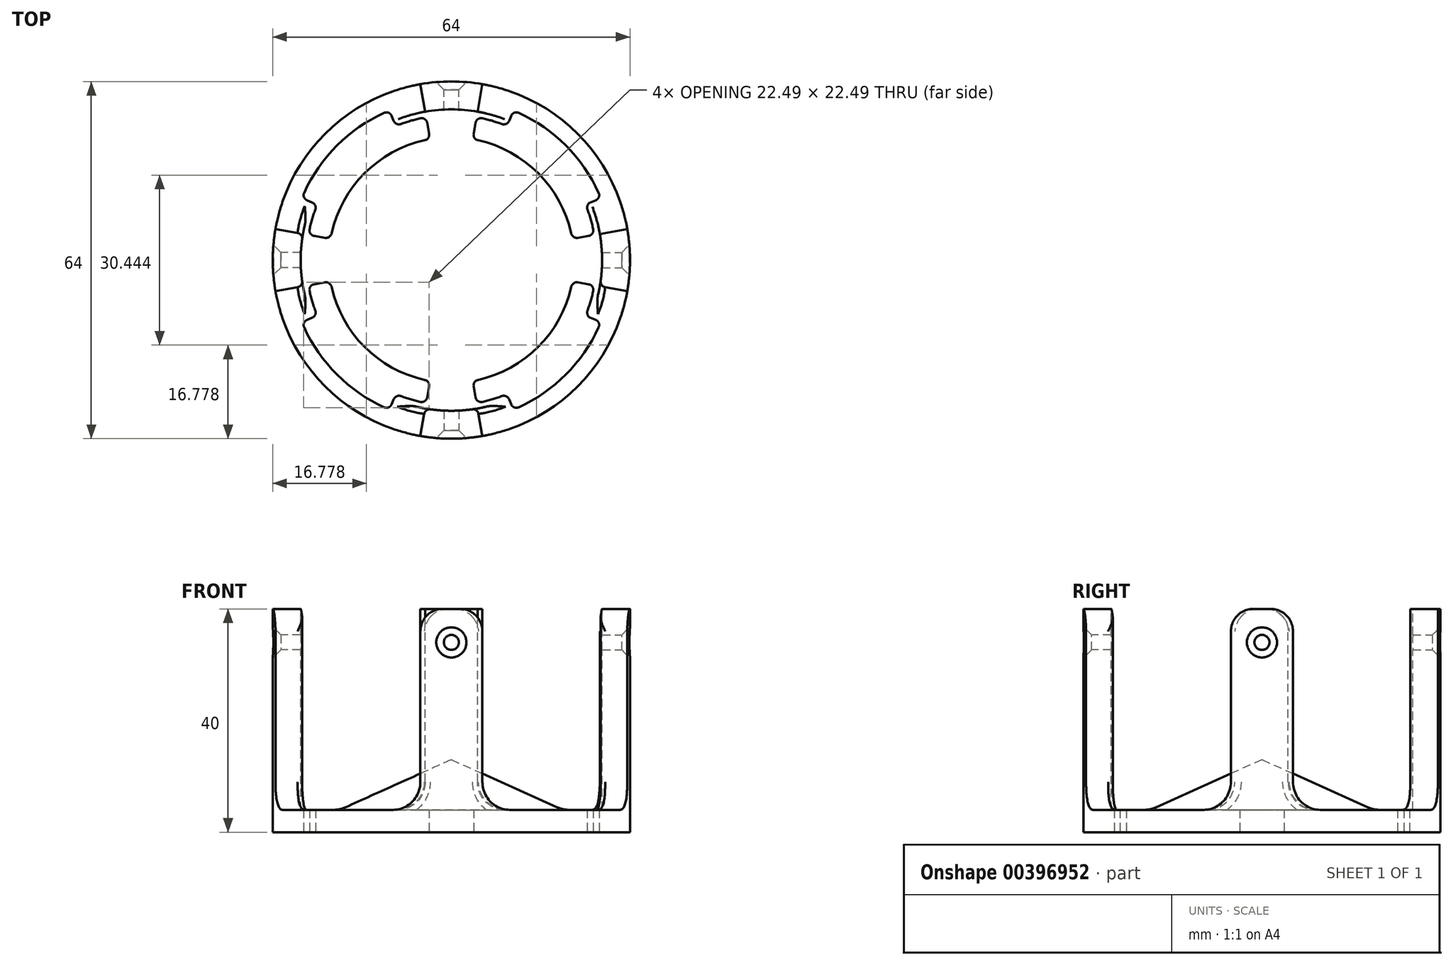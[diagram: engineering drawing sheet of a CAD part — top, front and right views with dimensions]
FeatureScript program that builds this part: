
annotation { "Feature Type Name" : "Feature", "Feature Type Description" : "" }
export const myFeature = defineFeature(function(context is Context, id is Id, definition is map)
    precondition{}
    {
        {
            var Q0;
            Q0=qCreatedBy(makeId("Front.planeOp"),FACE);
            var sketch = newSketch(context, id + "F0", { "sketchPlane" : qUnion([Q0])});
            skLineSegment(sketch, "E0", {"start": v(32, 0) * mm, "end": v(32, 40) * mm});
            skLineSegment(sketch, "E1", {"start": v(32, 40) * mm, "end": v(27, 40) * mm});
            skLineSegment(sketch, "E2", {"start": v(27, 40) * mm, "end": v(27, 4) * mm});
            skLineSegment(sketch, "E3", {"start": v(27, 4) * mm, "end": v(20, 4) * mm});
            skLineSegment(sketch, "E4", {"start": v(20, 4) * mm, "end": v(0, 13) * mm});
            skLineSegment(sketch, "E5", {"start": v(0, 13) * mm, "end": v(0, 0) * mm});
            skLineSegment(sketch, "E6", {"start": v(0, 0) * mm, "end": v(32, 0) * mm});
            skSolve(sketch);
        }
        {
            var Q0;
            Q0=makeQuery(id+"F0.imprint","IMPRINT",FACE,{"disambiguationData":[TD([[makeQuery(id+"F0.imprint","IMPRINT",EDGE,{"derivedFrom":sQuery(id+"F0.wireOp",EDGE,"E0")}),1.0]])]});
            var Q1;
            Q1=sQuery(id+"F0.wireOp",EDGE,"E5");
            revolve(context, id + "F1", {"entities" : qUnion([Q0]), "axis" : qUnion([Q1]), "revolveType" : RevolveType.FULL});
        }
        {
            var Q0;
            Q0=makeQuery(id+"F1.opRevolve","SWEPT_FACE",FACE,{"disambiguationData":[OSD([sQuery(id+"F0.wireOp",EDGE,"E1")])]});
            var sketch = newSketch(context, id + "F2", { "sketchPlane" : qUnion([Q0])});
            skLineSegment(sketch, "E7", {"start": v(-5.56, 31.51) * mm, "end": v(-4.69, 26.59) * mm});
            skLineSegment(sketch, "E8", {"start": v(4.69, 26.59) * mm, "end": v(5.56, 31.51) * mm});
            skLineSegment(sketch, "E9", {"start": v(31.51, 5.56) * mm, "end": v(26.59, 4.69) * mm});
            skLineSegment(sketch, "E10", {"start": v(31.51, -5.56) * mm, "end": v(26.59, -4.69) * mm});
            skLineSegment(sketch, "E11", {"start": v(4.69, -26.59) * mm, "end": v(5.56, -31.51) * mm});
            skLineSegment(sketch, "E12", {"start": v(-4.69, -26.59) * mm, "end": v(-5.56, -31.51) * mm});
            skLineSegment(sketch, "E13", {"start": v(-31.51, -5.56) * mm, "end": v(-26.59, -4.69) * mm});
            skLineSegment(sketch, "E14", {"start": v(-31.51, 5.56) * mm, "end": v(-26.59, 4.69) * mm});
            skArc(sketch, "E15", {"start": v(-5.56, 31.51) * mm, "mid": v(-22.63, 22.63) * mm, "end": v(-31.51, 5.56) * mm});
            skArc(sketch, "E16", {"start": v(-4.69, 26.59) * mm, "mid": v(-19.1, 19.1) * mm, "end": v(-26.59, 4.69) * mm});
            skArc(sketch, "E17.trimOffspring", {"start": v(26.59, 4.69) * mm, "mid": v(19.1, 19.1) * mm, "end": v(4.69, 26.59) * mm});
            skArc(sketch, "E18.trimOffspring", {"start": v(31.51, 5.56) * mm, "mid": v(22.63, 22.63) * mm, "end": v(5.56, 31.51) * mm});
            skArc(sketch, "E19.trimOffspring", {"start": v(4.69, -26.59) * mm, "mid": v(19.1, -19.1) * mm, "end": v(26.59, -4.69) * mm});
            skArc(sketch, "E20.trimOffspring", {"start": v(-31.51, -5.56) * mm, "mid": v(-22.63, -22.63) * mm, "end": v(-5.56, -31.51) * mm});
            skArc(sketch, "E21.trimOffspring", {"start": v(-26.59, -4.69) * mm, "mid": v(-19.1, -19.1) * mm, "end": v(-4.69, -26.59) * mm});
            skSolve(sketch);
        }
        {
            var Q0;
            Q0=makeQuery(id+"F2.imprint","IMPRINT",FACE,{"disambiguationData":[TD([[makeQuery(id+"F2.imprint","IMPRINT",EDGE,{"derivedFrom":sQuery(id+"F2.wireOp",EDGE,"E7")}),-1.0]])]});
            var Q1;
            Q1=makeQuery(id+"F2.imprint","IMPRINT",FACE,{"disambiguationData":[TD([[makeQuery(id+"F2.imprint","IMPRINT",EDGE,{"derivedFrom":sQuery(id+"F2.wireOp",EDGE,"E8")}),-1.0]])]});
            var Q2;
            {var subQ0=sQuery(id+"F2.wireOp",EDGE,"E10");Q2=makeQuery(id+"F2.imprint","IMPRINT",FACE,{"disambiguationData":[TD([[makeQuery(id+"F2.imprint","IMPRINT",EDGE,{"derivedFrom":subQ0}),1.0]])]});}
            var Q3;
            Q3=makeQuery(id+"F2.imprint","IMPRINT",FACE,{"disambiguationData":[TD([[makeQuery(id+"F2.imprint","IMPRINT",EDGE,{"derivedFrom":sQuery(id+"F2.wireOp",EDGE,"E12")}),-1.0]])]});
            var Q4;
            Q4=makeQuery(id+"F1.opRevolve","SWEPT_FACE",FACE,{"disambiguationData":[OSD([sQuery(id+"F0.wireOp",EDGE,"E3")])]});
            extrude(context, id + "F3", {"entities" : qUnion([Q0, Q1, Q2, Q3]), "operationType" : NewBodyOperationType.REMOVE, "endBound" : BoundingType.UP_TO_SURFACE, "oppositeDirection" : true, "endBoundEntityFace" : qUnion([Q4]), "depth" : 25 * mm});
        }
        {
            var Q0;
            Q0=makeQuery(id+"F3.boolean.opBoolean","COPY",EDGE,{"derivedFrom":makeQuery(id+"F3.opExtrude","CAP_EDGE",EDGE,{"disambiguationData":[OSD([sQuery(id+"F2.wireOp",EDGE,"E11")])],"isStart":false})});
            var Q1;
            Q1=makeQuery(id+"F3.boolean.opBoolean","COPY",EDGE,{"derivedFrom":makeQuery(id+"F3.opExtrude","CAP_EDGE",EDGE,{"disambiguationData":[OSD([sQuery(id+"F2.wireOp",EDGE,"E10")])],"isStart":false})});
            var Q2;
            Q2=makeQuery(id+"F3.boolean.opBoolean","COPY",EDGE,{"derivedFrom":makeQuery(id+"F3.opExtrude","CAP_EDGE",EDGE,{"disambiguationData":[OSD([sQuery(id+"F2.wireOp",EDGE,"E9")])],"isStart":false})});
            var Q3;
            Q3=makeQuery(id+"F3.boolean.opBoolean","COPY",EDGE,{"derivedFrom":makeQuery(id+"F3.opExtrude","CAP_EDGE",EDGE,{"disambiguationData":[OSD([sQuery(id+"F2.wireOp",EDGE,"E8")])],"isStart":false})});
            var Q4;
            Q4=makeQuery(id+"F3.boolean.opBoolean","COPY",EDGE,{"derivedFrom":makeQuery(id+"F3.opExtrude","CAP_EDGE",EDGE,{"disambiguationData":[OSD([sQuery(id+"F2.wireOp",EDGE,"E7")])],"isStart":false})});
            var Q5;
            Q5=makeQuery(id+"F3.boolean.opBoolean","COPY",EDGE,{"derivedFrom":makeQuery(id+"F3.opExtrude","CAP_EDGE",EDGE,{"disambiguationData":[OSD([sQuery(id+"F2.wireOp",EDGE,"E14")])],"isStart":false})});
            var Q6;
            Q6=makeQuery(id+"F3.boolean.opBoolean","COPY",EDGE,{"derivedFrom":makeQuery(id+"F3.opExtrude","CAP_EDGE",EDGE,{"disambiguationData":[OSD([sQuery(id+"F2.wireOp",EDGE,"E13")])],"isStart":false})});
            var Q7;
            Q7=makeQuery(id+"F3.boolean.opBoolean","COPY",EDGE,{"derivedFrom":makeQuery(id+"F3.opExtrude","CAP_EDGE",EDGE,{"disambiguationData":[OSD([sQuery(id+"F2.wireOp",EDGE,"E12")])],"isStart":false})});
            fillet(context, id + "F4", {"entities" : qUnion([Q0, Q1, Q2, Q3, Q4, Q5, Q6, Q7]), "radius" : 5 * mm, "tangentPropagation" : true, "allowEdgeOverflow" : false});
        }
        {
            var Q0;
            Q0=makeQuery(id+"F1.opRevolve","SWEPT_EDGE",EDGE,{"disambiguationData":[OSD([sQuery(id+"F0.wireOp",EDGE,"E3"),sQuery(id+"F0.wireOp",EDGE,"E4")])]});
            fillet(context, id + "F5", {"entities" : qUnion([Q0]), "radius" : 5 * mm, "tangentPropagation" : true, "allowEdgeOverflow" : false});
        }
        {
            var Q0;
            Q0=makeQuery(id+"F3.boolean.opBoolean","COPY",EDGE,{"derivedFrom":makeQuery(id+"F3.opExtrude","SWEPT_EDGE",EDGE,{"disambiguationData":[OSD([sQuery(id+"F0.wireOp",EDGE,"E0"),sQuery(id+"F0.wireOp",EDGE,"E1"),sQuery(id+"F2.wireOp",EDGE,"E13"),sQuery(id+"F2.wireOp",EDGE,"E20.trimOffspring")])]})});
            var Q1;
            Q1=makeQuery(id+"F3.boolean.opBoolean","COPY",EDGE,{"derivedFrom":makeQuery(id+"F3.opExtrude","SWEPT_EDGE",EDGE,{"disambiguationData":[OSD([sQuery(id+"F0.wireOp",EDGE,"E0"),sQuery(id+"F0.wireOp",EDGE,"E1"),sQuery(id+"F2.wireOp",EDGE,"E14"),sQuery(id+"F2.wireOp",EDGE,"E15")])]})});
            var Q2;
            Q2=makeQuery(id+"F3.boolean.opBoolean","COPY",EDGE,{"derivedFrom":makeQuery(id+"F3.opExtrude","SWEPT_EDGE",EDGE,{"disambiguationData":[OSD([sQuery(id+"F0.wireOp",EDGE,"E0"),sQuery(id+"F0.wireOp",EDGE,"E1"),sQuery(id+"F2.wireOp",EDGE,"E11")])]})});
            var Q3;
            Q3=makeQuery(id+"F3.boolean.opBoolean","COPY",EDGE,{"derivedFrom":makeQuery(id+"F3.opExtrude","SWEPT_EDGE",EDGE,{"disambiguationData":[OSD([sQuery(id+"F0.wireOp",EDGE,"E0"),sQuery(id+"F0.wireOp",EDGE,"E1"),sQuery(id+"F2.wireOp",EDGE,"E8"),sQuery(id+"F2.wireOp",EDGE,"E18.trimOffspring")])]})});
            var Q4;
            Q4=makeQuery(id+"F3.boolean.opBoolean","COPY",EDGE,{"derivedFrom":makeQuery(id+"F3.opExtrude","SWEPT_EDGE",EDGE,{"disambiguationData":[OSD([sQuery(id+"F0.wireOp",EDGE,"E1"),sQuery(id+"F0.wireOp",EDGE,"E2"),sQuery(id+"F2.wireOp",EDGE,"E11"),sQuery(id+"F2.wireOp",EDGE,"E19.trimOffspring")])]})});
            var Q5;
            Q5=makeQuery(id+"F3.boolean.opBoolean","COPY",EDGE,{"derivedFrom":makeQuery(id+"F3.opExtrude","SWEPT_EDGE",EDGE,{"disambiguationData":[OSD([sQuery(id+"F0.wireOp",EDGE,"E1"),sQuery(id+"F0.wireOp",EDGE,"E2"),sQuery(id+"F2.wireOp",EDGE,"E10"),sQuery(id+"F2.wireOp",EDGE,"E19.trimOffspring")])]})});
            var Q6;
            Q6=makeQuery(id+"F3.boolean.opBoolean","COPY",EDGE,{"derivedFrom":makeQuery(id+"F3.opExtrude","SWEPT_EDGE",EDGE,{"disambiguationData":[OSD([sQuery(id+"F0.wireOp",EDGE,"E1"),sQuery(id+"F0.wireOp",EDGE,"E2"),sQuery(id+"F2.wireOp",EDGE,"E8"),sQuery(id+"F2.wireOp",EDGE,"E17.trimOffspring")])]})});
            var Q7;
            Q7=makeQuery(id+"F3.boolean.opBoolean","COPY",EDGE,{"derivedFrom":makeQuery(id+"F3.opExtrude","SWEPT_EDGE",EDGE,{"disambiguationData":[OSD([sQuery(id+"F0.wireOp",EDGE,"E1"),sQuery(id+"F0.wireOp",EDGE,"E2"),sQuery(id+"F2.wireOp",EDGE,"E7"),sQuery(id+"F2.wireOp",EDGE,"E16")])]})});
            var Q8;
            Q8=makeQuery(id+"F3.boolean.opBoolean","COPY",EDGE,{"derivedFrom":makeQuery(id+"F3.opExtrude","SWEPT_EDGE",EDGE,{"disambiguationData":[OSD([sQuery(id+"F0.wireOp",EDGE,"E1"),sQuery(id+"F0.wireOp",EDGE,"E2"),sQuery(id+"F2.wireOp",EDGE,"E14"),sQuery(id+"F2.wireOp",EDGE,"E16")])]})});
            var Q9;
            Q9=makeQuery(id+"F3.boolean.opBoolean","COPY",EDGE,{"derivedFrom":makeQuery(id+"F3.opExtrude","SWEPT_EDGE",EDGE,{"disambiguationData":[OSD([sQuery(id+"F0.wireOp",EDGE,"E1"),sQuery(id+"F0.wireOp",EDGE,"E2"),sQuery(id+"F2.wireOp",EDGE,"E13"),sQuery(id+"F2.wireOp",EDGE,"E21.trimOffspring")])]})});
            var Q10;
            Q10=makeQuery(id+"F3.boolean.opBoolean","COPY",EDGE,{"derivedFrom":makeQuery(id+"F3.opExtrude","SWEPT_EDGE",EDGE,{"disambiguationData":[OSD([sQuery(id+"F0.wireOp",EDGE,"E1"),sQuery(id+"F0.wireOp",EDGE,"E2"),sQuery(id+"F2.wireOp",EDGE,"E12"),sQuery(id+"F2.wireOp",EDGE,"E21.trimOffspring")])]})});
            fillet(context, id + "F6", {"entities" : qUnion([Q0, Q1, Q2, Q3, Q4, Q5, Q6, Q7, Q8, Q9, Q10]), "radius" : 1 * mm, "tangentPropagation" : true, "allowEdgeOverflow" : false});
        }
        {
            var Q0;
            {var subQ0=sQuery(id+"F0.wireOp",EDGE,"E0");var subQ1=sQuery(id+"F0.wireOp",EDGE,"E1");Q0=makeQuery(id+"F3.boolean.opBoolean","SPLIT",EDGE,{"disambiguationData":[TD([makeQuery(id+"F3.opExtrude","SWEPT_FACE",FACE,{"disambiguationData":[OSD([sQuery(id+"F2.wireOp",EDGE,"E11")])]})])],"derivedFrom":makeQuery(id+"F1.opRevolve","SWEPT_EDGE",EDGE,{"disambiguationData":[OSD([subQ0,subQ1])]})});}
            cPoint(context, id + "F7", {"entities" : qUnion([Q0]), "parameter" : 0.5});
        }
        {
            var Q0;
            Q0=qCreatedBy(makeId("Front.planeOp"),FACE);
            var Q1;
            Q1 = qCreatedBy(id + "F7" ,VERTEX);
            cPlane(context, id + "F8", {"entities" : qUnion([Q0, Q1]), "cplaneType" : CPlaneType.PLANE_POINT, "offset" : 25 * mm, "width" : 150 * mm, "height" : 150 * mm});
        }
        {
            var Q0;
            {var subQ0=sQuery(id+"F0.wireOp",EDGE,"E0");var subQ1=sQuery(id+"F0.wireOp",EDGE,"E1");Q0=makeQuery(id+"F3.boolean.opBoolean","SPLIT",EDGE,{"disambiguationData":[TD([makeQuery(id+"F3.opExtrude","SWEPT_FACE",FACE,{"disambiguationData":[OSD([sQuery(id+"F2.wireOp",EDGE,"E9")])]})])],"derivedFrom":makeQuery(id+"F1.opRevolve","SWEPT_EDGE",EDGE,{"disambiguationData":[OSD([subQ0,subQ1])]})});}
            cPoint(context, id + "F9", {"entities" : qUnion([Q0]), "parameter" : 0.5});
        }
        {
            var Q0;
            Q0=qCreatedBy(makeId("Right.planeOp"),FACE);
            var Q1;
            Q1 = qCreatedBy(id + "F9" ,VERTEX);
            cPlane(context, id + "F10", {"entities" : qUnion([Q0, Q1]), "cplaneType" : CPlaneType.PLANE_POINT, "offset" : 25 * mm, "width" : 150 * mm, "height" : 150 * mm});
        }
        {
            var Q0;
            {var subQ0=sQuery(id+"F0.wireOp",EDGE,"E0");var subQ1=sQuery(id+"F0.wireOp",EDGE,"E1");Q0=makeQuery(id+"F3.boolean.opBoolean","SPLIT",EDGE,{"disambiguationData":[TD([makeQuery(id+"F3.opExtrude","SWEPT_FACE",FACE,{"disambiguationData":[OSD([sQuery(id+"F2.wireOp",EDGE,"E7")])]})])],"derivedFrom":makeQuery(id+"F1.opRevolve","SWEPT_EDGE",EDGE,{"disambiguationData":[OSD([subQ0,subQ1])]})});}
            cPoint(context, id + "F11", {"entities" : qUnion([Q0]), "parameter" : 0.5});
        }
        {
            var Q0;
            Q0=qCreatedBy(makeId("Front.planeOp"),FACE);
            var Q1;
            Q1 = qCreatedBy(id + "F11" ,VERTEX);
            cPlane(context, id + "F12", {"entities" : qUnion([Q0, Q1]), "cplaneType" : CPlaneType.PLANE_POINT, "offset" : 25 * mm, "width" : 150 * mm, "height" : 150 * mm});
        }
        {
            var Q0;
            {var subQ0=sQuery(id+"F0.wireOp",EDGE,"E0");var subQ1=sQuery(id+"F0.wireOp",EDGE,"E1");Q0=makeQuery(id+"F3.boolean.opBoolean","SPLIT",EDGE,{"disambiguationData":[TD([makeQuery(id+"F3.opExtrude","SWEPT_FACE",FACE,{"disambiguationData":[OSD([sQuery(id+"F2.wireOp",EDGE,"E13")])]})])],"derivedFrom":makeQuery(id+"F1.opRevolve","SWEPT_EDGE",EDGE,{"disambiguationData":[OSD([subQ0,subQ1])]})});}
            cPoint(context, id + "F13", {"entities" : qUnion([Q0]), "parameter" : 0.5});
        }
        {
            var Q0;
            Q0=qCreatedBy(makeId("Right.planeOp"),FACE);
            var Q1;
            Q1 = qCreatedBy(id + "F13" ,VERTEX);
            cPlane(context, id + "F14", {"entities" : qUnion([Q0, Q1]), "cplaneType" : CPlaneType.PLANE_POINT, "offset" : 25 * mm, "width" : 150 * mm, "height" : 150 * mm});
        }
        {
            var Q0;
            Q0=qCreatedBy(id+"F8.planeOp",FACE);
            var sketch = newSketch(context, id + "F15", { "sketchPlane" : qUnion([Q0])});
            skPoint(sketch, "E22", {"position": v(0, 34) * mm});
            skSolve(sketch);
        }
        {
            var Q0;
            Q0=qCreatedBy(id+"F10.planeOp",FACE);
            var sketch = newSketch(context, id + "F16", { "sketchPlane" : qUnion([Q0])});
            skPoint(sketch, "E23", {"position": v(0, 34) * mm});
            skSolve(sketch);
        }
        {
            var Q0;
            Q0=qCreatedBy(id+"F12.planeOp",FACE);
            var sketch = newSketch(context, id + "F17", { "sketchPlane" : qUnion([Q0])});
            skPoint(sketch, "E24", {"position": v(0, 34) * mm});
            skSolve(sketch);
        }
        {
            var Q0;
            Q0=qCreatedBy(id+"F14.planeOp",FACE);
            var sketch = newSketch(context, id + "F18", { "sketchPlane" : qUnion([Q0])});
            skPoint(sketch, "E25", {"position": v(0, 34) * mm});
            skSolve(sketch);
        }
        {
            var Q0;
            Q0=sQuery(id+"F16.wireOp",VERTEX,"E23");
            var Q1;
            Q1=makeQuery(id+"F1.opRevolve","SWEPT_BODY",BODY,{"disambiguationData":[OSD([sQuery(id+"F0.wireOp",EDGE,"E0"),sQuery(id+"F0.wireOp",EDGE,"E1"),sQuery(id+"F0.wireOp",EDGE,"E2"),sQuery(id+"F0.wireOp",EDGE,"E3"),sQuery(id+"F0.wireOp",EDGE,"E4"),sQuery(id+"F0.wireOp",EDGE,"E5"),sQuery(id+"F0.wireOp",EDGE,"E6")])]});
            hole(context, id + "F19", {"style" : HoleStyle.C_SINK, "endStyle" : HoleEndStyle.BLIND, "holeDiameter" : 2.7 * mm, "cSinkDiameter" : 5.4 * mm, "cSinkAngle" : 90 * degree, "holeDepth" : 12 * mm, "isTappedThrough" : true, "tappedDepth" : 12 * mm, "tapClearance" : 3, "locations" : qUnion([Q0]), "scope" : qUnion([Q1])});
        }
        {
            var Q0;
            Q0=sQuery(id+"F17.wireOp",VERTEX,"E24");
            var Q1;
            Q1=makeQuery(id+"F1.opRevolve","SWEPT_BODY",BODY,{"disambiguationData":[OSD([sQuery(id+"F0.wireOp",EDGE,"E0"),sQuery(id+"F0.wireOp",EDGE,"E1"),sQuery(id+"F0.wireOp",EDGE,"E2"),sQuery(id+"F0.wireOp",EDGE,"E3"),sQuery(id+"F0.wireOp",EDGE,"E4"),sQuery(id+"F0.wireOp",EDGE,"E5"),sQuery(id+"F0.wireOp",EDGE,"E6")])]});
            hole(context, id + "F20", {"style" : HoleStyle.C_SINK, "endStyle" : HoleEndStyle.BLIND, "oppositeDirection" : true, "holeDiameter" : 2.7 * mm, "cSinkDiameter" : 5.4 * mm, "cSinkAngle" : 90 * degree, "holeDepth" : 12 * mm, "isTappedThrough" : true, "tappedDepth" : 12 * mm, "tapClearance" : 3, "locations" : qUnion([Q0]), "scope" : qUnion([Q1])});
        }
        {
            var Q0;
            Q0=sQuery(id+"F18.wireOp",VERTEX,"E25");
            var Q1;
            Q1=makeQuery(id+"F1.opRevolve","SWEPT_BODY",BODY,{"disambiguationData":[OSD([sQuery(id+"F0.wireOp",EDGE,"E0"),sQuery(id+"F0.wireOp",EDGE,"E1"),sQuery(id+"F0.wireOp",EDGE,"E2"),sQuery(id+"F0.wireOp",EDGE,"E3"),sQuery(id+"F0.wireOp",EDGE,"E4"),sQuery(id+"F0.wireOp",EDGE,"E5"),sQuery(id+"F0.wireOp",EDGE,"E6")])]});
            hole(context, id + "F21", {"style" : HoleStyle.C_SINK, "endStyle" : HoleEndStyle.BLIND, "oppositeDirection" : true, "holeDiameter" : 2.7 * mm, "cSinkDiameter" : 5.4 * mm, "cSinkAngle" : 90 * degree, "holeDepth" : 12 * mm, "isTappedThrough" : true, "tappedDepth" : 12 * mm, "tapClearance" : 3, "locations" : qUnion([Q0]), "scope" : qUnion([Q1])});
        }
        {
            var Q0;
            Q0=sQuery(id+"F15.wireOp",VERTEX,"E22");
            var Q1;
            Q1=makeQuery(id+"F1.opRevolve","SWEPT_BODY",BODY,{"disambiguationData":[OSD([sQuery(id+"F0.wireOp",EDGE,"E0"),sQuery(id+"F0.wireOp",EDGE,"E1"),sQuery(id+"F0.wireOp",EDGE,"E2"),sQuery(id+"F0.wireOp",EDGE,"E3"),sQuery(id+"F0.wireOp",EDGE,"E4"),sQuery(id+"F0.wireOp",EDGE,"E5"),sQuery(id+"F0.wireOp",EDGE,"E6")])]});
            hole(context, id + "F22", {"style" : HoleStyle.C_SINK, "endStyle" : HoleEndStyle.BLIND, "holeDiameter" : 2.7 * mm, "cSinkDiameter" : 5.4 * mm, "cSinkAngle" : 90 * degree, "holeDepth" : 12 * mm, "isTappedThrough" : true, "tappedDepth" : 12 * mm, "tapClearance" : 3, "locations" : qUnion([Q0]), "scope" : qUnion([Q1])});
        }
        {
            var Q0;
            Q0=qCreatedBy(id+"F14.planeOp",FACE);
            var sketch = newSketch(context, id + "F23", { "sketchPlane" : qUnion([Q0])});
            skCircle(sketch, "E26", {"center": v(0, 34) * mm, "radius": 2.7 * mm});
            skSolve(sketch);
        }
        {
            var Q0;
            Q0=makeQuery(id+"F23.imprint","IMPRINT",FACE,{"disambiguationData":[TD([[makeQuery(id+"F23.imprint","IMPRINT",EDGE,{"derivedFrom":sQuery(id+"F23.wireOp",EDGE,"E26")}),1.0]])]});
            extrude(context, id + "F24", {"entities" : qUnion([Q0]), "operationType" : NewBodyOperationType.REMOVE, "oppositeDirection" : true, "depth" : 0.1 * mm});
        }
        {
            var Q0;
            Q0=qCreatedBy(id+"F12.planeOp",FACE);
            var sketch = newSketch(context, id + "F25", { "sketchPlane" : qUnion([Q0])});
            skCircle(sketch, "E27", {"center": v(0, 34) * mm, "radius": 2.7 * mm});
            skSolve(sketch);
        }
        {
            var Q0;
            Q0=makeQuery(id+"F25.imprint","IMPRINT",FACE,{"disambiguationData":[TD([[makeQuery(id+"F25.imprint","IMPRINT",EDGE,{"derivedFrom":sQuery(id+"F25.wireOp",EDGE,"E27")}),1.0]])]});
            extrude(context, id + "F26", {"entities" : qUnion([Q0]), "operationType" : NewBodyOperationType.REMOVE, "oppositeDirection" : true, "depth" : 0.1 * mm});
        }
        {
            var Q0;
            Q0=qCreatedBy(id+"F10.planeOp",FACE);
            var sketch = newSketch(context, id + "F27", { "sketchPlane" : qUnion([Q0])});
            skCircle(sketch, "E28", {"center": v(0, 34) * mm, "radius": 2.7 * mm});
            skSolve(sketch);
        }
        {
            var Q0;
            Q0=makeQuery(id+"F27.imprint","IMPRINT",FACE,{"disambiguationData":[TD([[makeQuery(id+"F27.imprint","IMPRINT",EDGE,{"derivedFrom":sQuery(id+"F27.wireOp",EDGE,"E28")}),1.0]])]});
            extrude(context, id + "F28", {"entities" : qUnion([Q0]), "operationType" : NewBodyOperationType.REMOVE, "depth" : 0.1 * mm});
        }
        {
            var Q0;
            Q0=qCreatedBy(id+"F8.planeOp",FACE);
            var sketch = newSketch(context, id + "F29", { "sketchPlane" : qUnion([Q0])});
            skCircle(sketch, "E29", {"center": v(0, 34) * mm, "radius": 2.7 * mm});
            skSolve(sketch);
        }
        {
            var Q0;
            Q0=makeQuery(id+"F29.imprint","IMPRINT",FACE,{"disambiguationData":[TD([[makeQuery(id+"F29.imprint","IMPRINT",EDGE,{"derivedFrom":sQuery(id+"F29.wireOp",EDGE,"E29")}),1.0]])]});
            extrude(context, id + "F30", {"entities" : qUnion([Q0]), "operationType" : NewBodyOperationType.REMOVE, "depth" : 0.1 * mm});
        }
        {
            var Q0;
            Q0=makeQuery(id+"F3.boolean.opBoolean","COPY",EDGE,{"derivedFrom":makeQuery(id+"F3.opExtrude","CAP_EDGE",EDGE,{"disambiguationData":[OSD([sQuery(id+"F2.wireOp",EDGE,"E12")])],"isStart":true})});
            var Q1;
            Q1=makeQuery(id+"F3.boolean.opBoolean","COPY",EDGE,{"derivedFrom":makeQuery(id+"F3.opExtrude","CAP_EDGE",EDGE,{"disambiguationData":[OSD([sQuery(id+"F2.wireOp",EDGE,"E11")])],"isStart":true})});
            var Q2;
            Q2=makeQuery(id+"F3.boolean.opBoolean","COPY",EDGE,{"derivedFrom":makeQuery(id+"F3.opExtrude","CAP_EDGE",EDGE,{"disambiguationData":[OSD([sQuery(id+"F2.wireOp",EDGE,"E10")])],"isStart":true})});
            var Q3;
            Q3=makeQuery(id+"F3.boolean.opBoolean","COPY",EDGE,{"derivedFrom":makeQuery(id+"F3.opExtrude","CAP_EDGE",EDGE,{"disambiguationData":[OSD([sQuery(id+"F2.wireOp",EDGE,"E9")])],"isStart":true})});
            var Q4;
            Q4=makeQuery(id+"F3.boolean.opBoolean","COPY",EDGE,{"derivedFrom":makeQuery(id+"F3.opExtrude","CAP_EDGE",EDGE,{"disambiguationData":[OSD([sQuery(id+"F2.wireOp",EDGE,"E8")])],"isStart":true})});
            var Q5;
            Q5=makeQuery(id+"F3.boolean.opBoolean","COPY",EDGE,{"derivedFrom":makeQuery(id+"F3.opExtrude","CAP_EDGE",EDGE,{"disambiguationData":[OSD([sQuery(id+"F2.wireOp",EDGE,"E7")])],"isStart":true})});
            var Q6;
            Q6=makeQuery(id+"F3.boolean.opBoolean","COPY",EDGE,{"derivedFrom":makeQuery(id+"F3.opExtrude","CAP_EDGE",EDGE,{"disambiguationData":[OSD([sQuery(id+"F2.wireOp",EDGE,"E13")])],"isStart":true})});
            var Q7;
            Q7=makeQuery(id+"F3.boolean.opBoolean","COPY",EDGE,{"derivedFrom":makeQuery(id+"F3.opExtrude","CAP_EDGE",EDGE,{"disambiguationData":[OSD([sQuery(id+"F2.wireOp",EDGE,"E14")])],"isStart":true})});
            fillet(context, id + "F31", {"entities" : qUnion([Q0, Q1, Q2, Q3, Q4, Q5, Q6, Q7]), "radius" : 4 * mm, "allowEdgeOverflow" : false});
        }
        {
            var Q0;
            Q0=qCreatedBy(makeId("Top.planeOp"),FACE);
            var sketch = newSketch(context, id + "F32", { "sketchPlane" : qUnion([Q0])});
            skArc(sketch, "E30", {"start": v(-12.05, 26.38) * mm, "mid": v(-20.5, 20.5) * mm, "end": v(-26.38, 12.05) * mm});
            skArc(sketch, "E31", {"start": v(-4.76, 21.48) * mm, "mid": v(-15.56, 15.56) * mm, "end": v(-21.48, 4.76) * mm});
            skLineSegment(sketch, "E32", {"start": v(-4, 22.63) * mm, "end": v(-4.34, 24.6) * mm});
            skLineSegment(sketch, "E33", {"start": v(-22.63, 4) * mm, "end": v(-24.6, 4.34) * mm});
            skArc(sketch, "E34", {"start": v(-25.4, 5.54) * mm, "mid": v(-24.95, 7.31) * mm, "end": v(-24.37, 9.05) * mm});
            skArc(sketch, "E35", {"start": v(-5.54, 25.4) * mm, "mid": v(-7.31, 24.95) * mm, "end": v(-9.05, 24.37) * mm});
            skLineSegment(sketch, "E36.trimOffspring", {"start": v(-10.33, 24.93) * mm, "end": v(-10.7, 25.85) * mm});
            skLineSegment(sketch, "E37.trimOffspring", {"start": v(-24.93, 10.33) * mm, "end": v(-25.85, 10.7) * mm});
            skPoint(sketch, "E38.visualSharp", {"position": v(-11.1, 26.8) * mm});
            skArc(sketch, "E38.filletArc", {"start": v(-10.7, 25.85) * mm, "mid": v(-11.27, 26.4) * mm, "end": v(-12.05, 26.38) * mm});
            skPoint(sketch, "E39.visualSharp", {"position": v(-9.95, 24.02) * mm});
            skArc(sketch, "E39.filletArc", {"start": v(-10.33, 24.93) * mm, "mid": v(-9.8, 24.4) * mm, "end": v(-9.05, 24.37) * mm});
            skPoint(sketch, "E40.visualSharp", {"position": v(-4.51, 25.6) * mm});
            skArc(sketch, "E40.filletArc", {"start": v(-4.34, 24.6) * mm, "mid": v(-4.77, 25.26) * mm, "end": v(-5.54, 25.4) * mm});
            skPoint(sketch, "E41.visualSharp", {"position": v(-26.8, 11.1) * mm});
            skArc(sketch, "E41.filletArc", {"start": v(-26.38, 12.05) * mm, "mid": v(-26.4, 11.27) * mm, "end": v(-25.85, 10.7) * mm});
            skPoint(sketch, "E42.visualSharp", {"position": v(-24.02, 9.95) * mm});
            skArc(sketch, "E42.filletArc", {"start": v(-24.37, 9.05) * mm, "mid": v(-24.4, 9.8) * mm, "end": v(-24.93, 10.33) * mm});
            skPoint(sketch, "E43.visualSharp", {"position": v(-25.6, 4.51) * mm});
            skArc(sketch, "E43.filletArc", {"start": v(-25.4, 5.54) * mm, "mid": v(-25.26, 4.77) * mm, "end": v(-24.6, 4.34) * mm});
            skPoint(sketch, "E44.visualSharp", {"position": v(-3.82, 21.67) * mm});
            skPoint(sketch, "E45.visualSharp", {"position": v(-21.67, 3.82) * mm});
            skArc(sketch, "E46.filletArc", {"start": v(-4.76, 21.48) * mm, "mid": v(-4.14, 21.9) * mm, "end": v(-4, 22.63) * mm});
            skArc(sketch, "E47.filletArc", {"start": v(-22.63, 4) * mm, "mid": v(-21.9, 4.14) * mm, "end": v(-21.48, 4.76) * mm});
            skPoint(sketch, "E48.1.0", {"position": v(-24.02, -9.95) * mm});
            skPoint(sketch, "E48.1.1", {"position": v(-3.82, -21.67) * mm});
            skPoint(sketch, "E48.1.2", {"position": v(-9.95, -24.02) * mm});
            skPoint(sketch, "E48.1.3", {"position": v(-4.51, -25.6) * mm});
            skPoint(sketch, "E48.1.4", {"position": v(-11.1, -26.8) * mm});
            skPoint(sketch, "E48.1.5", {"position": v(-21.67, -3.82) * mm});
            skPoint(sketch, "E48.1.6", {"position": v(-26.8, -11.1) * mm});
            skArc(sketch, "E48.1.7", {"start": v(-21.48, -4.76) * mm, "mid": v(-15.56, -15.56) * mm, "end": v(-4.76, -21.48) * mm});
            skArc(sketch, "E48.1.8", {"start": v(-26.38, -12.05) * mm, "mid": v(-20.5, -20.5) * mm, "end": v(-12.05, -26.38) * mm});
            skPoint(sketch, "E48.1.9", {"position": v(-25.6, -4.51) * mm});
            skArc(sketch, "E48.1.10", {"start": v(-25.4, -5.54) * mm, "mid": v(-24.95, -7.31) * mm, "end": v(-24.37, -9.05) * mm});
            skLineSegment(sketch, "E48.1.11", {"start": v(-24.93, -10.33) * mm, "end": v(-25.85, -10.7) * mm});
            skArc(sketch, "E48.1.12", {"start": v(-5.54, -25.4) * mm, "mid": v(-4.77, -25.26) * mm, "end": v(-4.34, -24.6) * mm});
            skArc(sketch, "E48.1.13", {"start": v(-5.54, -25.4) * mm, "mid": v(-7.31, -24.95) * mm, "end": v(-9.05, -24.37) * mm});
            skArc(sketch, "E48.1.14", {"start": v(-24.93, -10.33) * mm, "mid": v(-24.4, -9.8) * mm, "end": v(-24.37, -9.05) * mm});
            skLineSegment(sketch, "E48.1.15", {"start": v(-22.63, -4) * mm, "end": v(-24.6, -4.34) * mm});
            skArc(sketch, "E48.1.16", {"start": v(-12.05, -26.38) * mm, "mid": v(-11.27, -26.4) * mm, "end": v(-10.7, -25.85) * mm});
            skArc(sketch, "E48.1.17", {"start": v(-25.85, -10.7) * mm, "mid": v(-26.4, -11.27) * mm, "end": v(-26.38, -12.05) * mm});
            skArc(sketch, "E48.1.18", {"start": v(-24.6, -4.34) * mm, "mid": v(-25.26, -4.77) * mm, "end": v(-25.4, -5.54) * mm});
            skArc(sketch, "E48.1.19", {"start": v(-21.48, -4.76) * mm, "mid": v(-21.9, -4.14) * mm, "end": v(-22.63, -4) * mm});
            skLineSegment(sketch, "E48.1.20", {"start": v(-4, -22.63) * mm, "end": v(-4.34, -24.6) * mm});
            skArc(sketch, "E48.1.21", {"start": v(-9.05, -24.37) * mm, "mid": v(-9.8, -24.4) * mm, "end": v(-10.33, -24.93) * mm});
            skLineSegment(sketch, "E48.1.22", {"start": v(-10.33, -24.93) * mm, "end": v(-10.7, -25.85) * mm});
            skArc(sketch, "E48.1.23", {"start": v(-4, -22.63) * mm, "mid": v(-4.14, -21.9) * mm, "end": v(-4.76, -21.48) * mm});
            skPoint(sketch, "E48.2.0", {"position": v(9.95, -24.02) * mm});
            skPoint(sketch, "E48.2.1", {"position": v(21.67, -3.82) * mm});
            skPoint(sketch, "E48.2.2", {"position": v(24.02, -9.95) * mm});
            skPoint(sketch, "E48.2.3", {"position": v(25.6, -4.51) * mm});
            skPoint(sketch, "E48.2.4", {"position": v(26.8, -11.1) * mm});
            skPoint(sketch, "E48.2.5", {"position": v(3.82, -21.67) * mm});
            skPoint(sketch, "E48.2.6", {"position": v(11.1, -26.8) * mm});
            skArc(sketch, "E48.2.7", {"start": v(4.76, -21.48) * mm, "mid": v(15.56, -15.56) * mm, "end": v(21.48, -4.76) * mm});
            skArc(sketch, "E48.2.8", {"start": v(12.05, -26.38) * mm, "mid": v(20.5, -20.5) * mm, "end": v(26.38, -12.05) * mm});
            skPoint(sketch, "E48.2.9", {"position": v(4.51, -25.6) * mm});
            skArc(sketch, "E48.2.10", {"start": v(5.54, -25.4) * mm, "mid": v(7.31, -24.95) * mm, "end": v(9.05, -24.37) * mm});
            skLineSegment(sketch, "E48.2.11", {"start": v(10.33, -24.93) * mm, "end": v(10.7, -25.85) * mm});
            skArc(sketch, "E48.2.12", {"start": v(25.4, -5.54) * mm, "mid": v(25.26, -4.77) * mm, "end": v(24.6, -4.34) * mm});
            skArc(sketch, "E48.2.13", {"start": v(25.4, -5.54) * mm, "mid": v(24.95, -7.31) * mm, "end": v(24.37, -9.05) * mm});
            skArc(sketch, "E48.2.14", {"start": v(10.33, -24.93) * mm, "mid": v(9.8, -24.4) * mm, "end": v(9.05, -24.37) * mm});
            skLineSegment(sketch, "E48.2.15", {"start": v(4, -22.63) * mm, "end": v(4.34, -24.6) * mm});
            skArc(sketch, "E48.2.16", {"start": v(26.38, -12.05) * mm, "mid": v(26.4, -11.27) * mm, "end": v(25.85, -10.7) * mm});
            skArc(sketch, "E48.2.17", {"start": v(10.7, -25.85) * mm, "mid": v(11.27, -26.4) * mm, "end": v(12.05, -26.38) * mm});
            skArc(sketch, "E48.2.18", {"start": v(4.34, -24.6) * mm, "mid": v(4.77, -25.26) * mm, "end": v(5.54, -25.4) * mm});
            skArc(sketch, "E48.2.19", {"start": v(4.76, -21.48) * mm, "mid": v(4.14, -21.9) * mm, "end": v(4, -22.63) * mm});
            skLineSegment(sketch, "E48.2.20", {"start": v(22.63, -4) * mm, "end": v(24.6, -4.34) * mm});
            skArc(sketch, "E48.2.21", {"start": v(24.37, -9.05) * mm, "mid": v(24.4, -9.8) * mm, "end": v(24.93, -10.33) * mm});
            skLineSegment(sketch, "E48.2.22", {"start": v(24.93, -10.33) * mm, "end": v(25.85, -10.7) * mm});
            skArc(sketch, "E48.2.23", {"start": v(22.63, -4) * mm, "mid": v(21.9, -4.14) * mm, "end": v(21.48, -4.76) * mm});
            skPoint(sketch, "E49.0.3.0", {"position": v(4.51, 25.6) * mm});
            skPoint(sketch, "E49.1.3.0", {"position": v(3.82, 21.67) * mm});
            skPoint(sketch, "E49.2.3.0", {"position": v(9.95, 24.02) * mm});
            skPoint(sketch, "E49.3.3.0", {"position": v(24.02, 9.95) * mm});
            skPoint(sketch, "E49.4.3.0", {"position": v(11.1, 26.8) * mm});
            skPoint(sketch, "E49.5.3.0", {"position": v(21.67, 3.82) * mm});
            skPoint(sketch, "E49.6.3.0", {"position": v(26.8, 11.1) * mm});
            skArc(sketch, "E49.7.3.0", {"start": v(21.48, 4.76) * mm, "mid": v(15.56, 15.56) * mm, "end": v(4.76, 21.48) * mm});
            skArc(sketch, "E49.11.3.0", {"start": v(26.38, 12.05) * mm, "mid": v(20.5, 20.5) * mm, "end": v(12.05, 26.38) * mm});
            skPoint(sketch, "E49.15.3.0", {"position": v(25.6, 4.51) * mm});
            skArc(sketch, "E49.16.3.0", {"start": v(25.4, 5.54) * mm, "mid": v(24.95, 7.31) * mm, "end": v(24.37, 9.05) * mm});
            skLineSegment(sketch, "E49.20.3.0", {"start": v(24.93, 10.33) * mm, "end": v(25.85, 10.7) * mm});
            skArc(sketch, "E49.23.3.0", {"start": v(5.54, 25.4) * mm, "mid": v(4.77, 25.26) * mm, "end": v(4.34, 24.6) * mm});
            skArc(sketch, "E49.27.3.0", {"start": v(5.54, 25.4) * mm, "mid": v(7.31, 24.95) * mm, "end": v(9.05, 24.37) * mm});
            skArc(sketch, "E49.31.3.0", {"start": v(24.93, 10.33) * mm, "mid": v(24.4, 9.8) * mm, "end": v(24.37, 9.05) * mm});
            skLineSegment(sketch, "E49.35.3.0", {"start": v(22.63, 4) * mm, "end": v(24.6, 4.34) * mm});
            skArc(sketch, "E49.38.3.0", {"start": v(12.05, 26.38) * mm, "mid": v(11.27, 26.4) * mm, "end": v(10.7, 25.85) * mm});
            skArc(sketch, "E49.42.3.0", {"start": v(25.85, 10.7) * mm, "mid": v(26.4, 11.27) * mm, "end": v(26.38, 12.05) * mm});
            skArc(sketch, "E49.46.3.0", {"start": v(24.6, 4.34) * mm, "mid": v(25.26, 4.77) * mm, "end": v(25.4, 5.54) * mm});
            skArc(sketch, "E49.50.3.0", {"start": v(21.48, 4.76) * mm, "mid": v(21.9, 4.14) * mm, "end": v(22.63, 4) * mm});
            skLineSegment(sketch, "E49.54.3.0", {"start": v(4, 22.63) * mm, "end": v(4.34, 24.6) * mm});
            skArc(sketch, "E49.57.3.0", {"start": v(9.05, 24.37) * mm, "mid": v(9.8, 24.4) * mm, "end": v(10.33, 24.93) * mm});
            skLineSegment(sketch, "E49.61.3.0", {"start": v(10.33, 24.93) * mm, "end": v(10.7, 25.85) * mm});
            skArc(sketch, "E49.64.3.0", {"start": v(4, 22.63) * mm, "mid": v(4.14, 21.9) * mm, "end": v(4.76, 21.48) * mm});
            skSolve(sketch);
        }
        {
            var Q0;
            Q0 = qSketchRegion(id + "F32", true);
            extrude(context, id + "F33", {"entities" : qUnion([Q0]), "operationType" : NewBodyOperationType.REMOVE, "endBound" : BoundingType.THROUGH_ALL, "depth" : 25 * mm});
        }
    });
